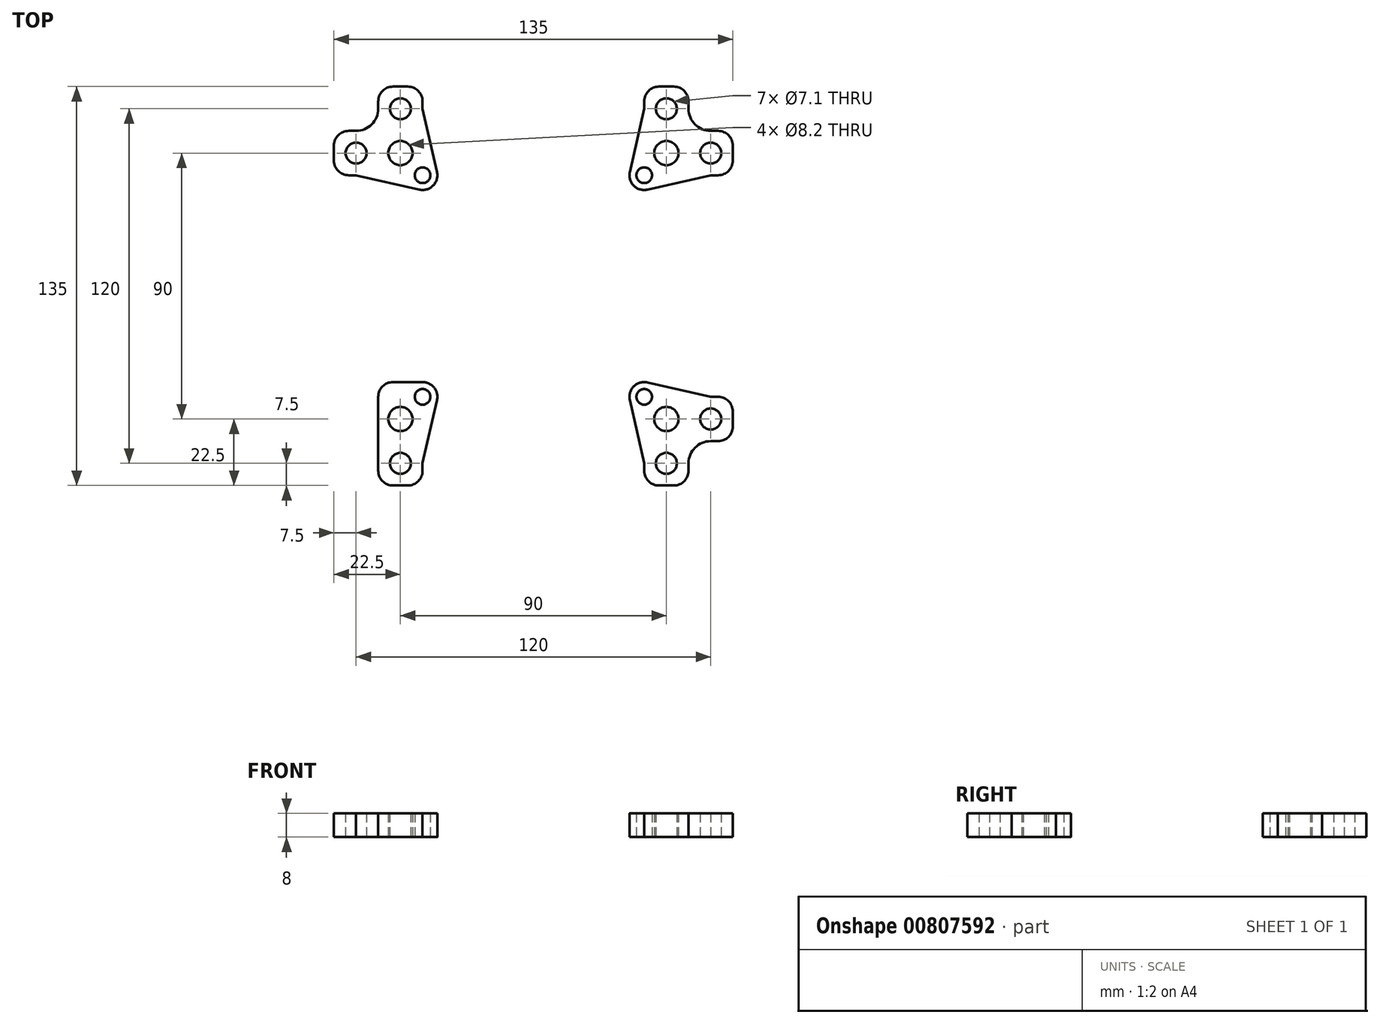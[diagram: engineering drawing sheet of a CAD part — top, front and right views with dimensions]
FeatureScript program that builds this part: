
annotation { "Feature Type Name" : "Feature", "Feature Type Description" : "" }
export const myFeature = defineFeature(function(context is Context, id is Id, definition is map)
    precondition{}
    {
        {
            var Q0;
            Q0=qCreatedBy(makeId("Top.planeOp"),FACE);
            var sketch = newSketch(context, id + "F0", { "sketchPlane" : qUnion([Q0])});
            skLineSegment(sketch, "E0.bottom", {"start": v(45, 45) * mm, "end": v(-45, 45) * mm, "construction": true});
            skLineSegment(sketch, "E0.top", {"start": v(45, -45) * mm, "end": v(-45, -45) * mm, "construction": true});
            skLineSegment(sketch, "E0.left", {"start": v(45, 45) * mm, "end": v(45, -45) * mm, "construction": true});
            skLineSegment(sketch, "E0.right", {"start": v(-45, 45) * mm, "end": v(-45, -45) * mm, "construction": true});
            skPoint(sketch, "E0.middle", {"position": v(0, 0) * mm});
            skCircle(sketch, "E1", {"center": v(-45, 45) * mm, "radius": 4.1 * mm});
            skCircle(sketch, "E2", {"center": v(45, 45) * mm, "radius": 4.1 * mm});
            skCircle(sketch, "E3", {"center": v(-45, -45) * mm, "radius": 4.1 * mm});
            skCircle(sketch, "E4", {"center": v(45, -45) * mm, "radius": 4.1 * mm});
            skLineSegment(sketch, "E5.bottom", {"start": v(37.5, 37.5) * mm, "end": v(-37.5, 37.5) * mm, "construction": true});
            skLineSegment(sketch, "E5.top", {"start": v(37.5, -37.5) * mm, "end": v(-37.5, -37.5) * mm, "construction": true});
            skLineSegment(sketch, "E5.left", {"start": v(37.5, 37.5) * mm, "end": v(37.5, -37.5) * mm, "construction": true});
            skLineSegment(sketch, "E5.right", {"start": v(-37.5, 37.5) * mm, "end": v(-37.5, -37.5) * mm, "construction": true});
            skCircle(sketch, "E6", {"center": v(-37.5, 37.5) * mm, "radius": 2.65 * mm});
            skCircle(sketch, "E7", {"center": v(37.5, 37.5) * mm, "radius": 2.65 * mm});
            skCircle(sketch, "E8", {"center": v(-37.5, -37.5) * mm, "radius": 2.65 * mm});
            skCircle(sketch, "E9", {"center": v(37.5, -37.5) * mm, "radius": 2.65 * mm});
            skCircle(sketch, "E10", {"center": v(-45, 60) * mm, "radius": 3.55 * mm});
            skCircle(sketch, "E11", {"center": v(-60, 45) * mm, "radius": 3.55 * mm});
            skCircle(sketch, "E12.MirrorC", {"center": v(45, 60) * mm, "radius": 3.55 * mm});
            skCircle(sketch, "E13.MirrorC", {"center": v(60, 45) * mm, "radius": 3.55 * mm});
            skCircle(sketch, "E14.MirrorC", {"center": v(-45, -60) * mm, "radius": 3.55 * mm});
            skCircle(sketch, "E15.MirrorC", {"center": v(45, -60) * mm, "radius": 3.55 * mm});
            skCircle(sketch, "E16.MirrorC", {"center": v(60, -45) * mm, "radius": 3.55 * mm});
            skLineSegment(sketch, "E17.bottom", {"start": v(-30, 52.5) * mm, "end": v(30, 52.5) * mm, "construction": true});
            skLineSegment(sketch, "E17.top", {"start": v(-30, -52.5) * mm, "end": v(30, -52.5) * mm, "construction": true});
            skLineSegment(sketch, "E17.left", {"start": v(-52.5, 30) * mm, "end": v(-52.5, -52.5) * mm, "construction": true});
            skLineSegment(sketch, "E17.right", {"start": v(52.5, 30) * mm, "end": v(52.5, -30) * mm, "construction": true});
            skLineSegment(sketch, "E18.top", {"start": v(-47.5, 67.5) * mm, "end": v(-42.5, 67.5) * mm});
            skLineSegment(sketch, "E18.left", {"start": v(-52.5, 60) * mm, "end": v(-52.5, 62.5) * mm});
            skLineSegment(sketch, "E18.right", {"start": v(-37.5, 60) * mm, "end": v(-37.5, 62.5) * mm});
            skLineSegment(sketch, "E19.bottom", {"start": v(-60, 52.5) * mm, "end": v(-62.5, 52.5) * mm});
            skLineSegment(sketch, "E19.top", {"start": v(-60, 37.5) * mm, "end": v(-62.5, 37.5) * mm});
            skLineSegment(sketch, "E19.right", {"start": v(-67.5, 47.5) * mm, "end": v(-67.5, 42.5) * mm});
            skLineSegment(sketch, "E20.MirrorCS", {"start": v(37.5, 60) * mm, "end": v(37.5, 62.5) * mm});
            skLineSegment(sketch, "E21.MirrorCS", {"start": v(47.5, 67.5) * mm, "end": v(42.5, 67.5) * mm});
            skLineSegment(sketch, "E22.MirrorCS", {"start": v(52.5, 60) * mm, "end": v(52.5, 62.5) * mm});
            skLineSegment(sketch, "E23.MirrorCS", {"start": v(60, 52.5) * mm, "end": v(62.5, 52.5) * mm});
            skLineSegment(sketch, "E24.MirrorCS", {"start": v(60, 37.5) * mm, "end": v(62.5, 37.5) * mm});
            skLineSegment(sketch, "E25.MirrorCS", {"start": v(67.5, 47.5) * mm, "end": v(67.5, 42.5) * mm});
            skLineSegment(sketch, "E26.MirrorCS", {"start": v(-52.5, -52.5) * mm, "end": v(-52.5, -62.5) * mm});
            skLineSegment(sketch, "E27.MirrorCS", {"start": v(-47.5, -67.5) * mm, "end": v(-42.5, -67.5) * mm});
            skLineSegment(sketch, "E28.MirrorCS", {"start": v(-37.5, -60) * mm, "end": v(-37.5, -62.5) * mm});
            skLineSegment(sketch, "E29.MirrorCS", {"start": v(37.5, -60) * mm, "end": v(37.5, -62.5) * mm});
            skLineSegment(sketch, "E30.MirrorCS", {"start": v(47.5, -67.5) * mm, "end": v(42.5, -67.5) * mm});
            skLineSegment(sketch, "E31.MirrorCS", {"start": v(52.5, -60) * mm, "end": v(52.5, -62.5) * mm});
            skLineSegment(sketch, "E32.MirrorCS", {"start": v(60, -52.5) * mm, "end": v(62.5, -52.5) * mm});
            skLineSegment(sketch, "E33.MirrorCS", {"start": v(67.5, -47.5) * mm, "end": v(67.5, -42.5) * mm});
            skLineSegment(sketch, "E34.MirrorCS", {"start": v(60, -37.5) * mm, "end": v(62.5, -37.5) * mm});
            skPoint(sketch, "E35.orphan", {"position": v(52.5, 52.5) * mm});
            skPoint(sketch, "E36.orphan", {"position": v(52.5, -52.5) * mm});
            skPoint(sketch, "E37.visualSharp", {"position": v(-52.5, 52.5) * mm});
            skArc(sketch, "E37.filletArc", {"start": v(-60, 52.5) * mm, "mid": v(-54.7, 54.7) * mm, "end": v(-52.5, 60) * mm});
            skArc(sketch, "E38.filletArc", {"start": v(52.5, 60) * mm, "mid": v(54.7, 54.7) * mm, "end": v(60, 52.5) * mm});
            skPoint(sketch, "E39.visualSharp", {"position": v(52.5, 37.5) * mm});
            skArc(sketch, "E39.filletArc", {"start": v(60, 37.5) * mm, "mid": v(54.7, 35.3) * mm, "end": v(52.5, 30) * mm, "construction": true});
            skPoint(sketch, "E40.visualSharp", {"position": v(52.5, -37.5) * mm});
            skArc(sketch, "E40.filletArc", {"start": v(52.5, -30) * mm, "mid": v(54.7, -35.3) * mm, "end": v(60, -37.5) * mm, "construction": true});
            skArc(sketch, "E41.filletArc", {"start": v(60, -52.5) * mm, "mid": v(54.7, -54.7) * mm, "end": v(52.5, -60) * mm});
            skPoint(sketch, "E42.visualSharp", {"position": v(37.5, -52.5) * mm});
            skArc(sketch, "E42.filletArc", {"start": v(37.5, -60) * mm, "mid": v(35.3, -54.7) * mm, "end": v(30, -52.5) * mm, "construction": true});
            skPoint(sketch, "E43.visualSharp", {"position": v(-37.5, -52.5) * mm});
            skArc(sketch, "E43.filletArc", {"start": v(-30, -52.5) * mm, "mid": v(-35.3, -54.7) * mm, "end": v(-37.5, -60) * mm, "construction": true});
            skPoint(sketch, "E44.visualSharp", {"position": v(-52.5, 37.5) * mm});
            skArc(sketch, "E44.filletArc", {"start": v(-52.5, 30) * mm, "mid": v(-54.7, 35.3) * mm, "end": v(-60, 37.5) * mm, "construction": true});
            skPoint(sketch, "E45.visualSharp", {"position": v(-37.5, 52.5) * mm});
            skArc(sketch, "E45.filletArc", {"start": v(-37.5, 60) * mm, "mid": v(-35.3, 54.7) * mm, "end": v(-30, 52.5) * mm, "construction": true});
            skPoint(sketch, "E46.visualSharp", {"position": v(37.5, 52.5) * mm});
            skArc(sketch, "E46.filletArc", {"start": v(30, 52.5) * mm, "mid": v(35.3, 54.7) * mm, "end": v(37.5, 60) * mm, "construction": true});
            skPoint(sketch, "E47.visualSharp", {"position": v(-52.5, -67.5) * mm});
            skArc(sketch, "E47.filletArc", {"start": v(-52.5, -62.5) * mm, "mid": v(-51.04, -66.04) * mm, "end": v(-47.5, -67.5) * mm});
            skPoint(sketch, "E48.visualSharp", {"position": v(-37.5, -67.5) * mm});
            skArc(sketch, "E48.filletArc", {"start": v(-42.5, -67.5) * mm, "mid": v(-38.96, -66.04) * mm, "end": v(-37.5, -62.5) * mm});
            skPoint(sketch, "E49.visualSharp", {"position": v(37.5, -67.5) * mm});
            skArc(sketch, "E49.filletArc", {"start": v(37.5, -62.5) * mm, "mid": v(38.96, -66.04) * mm, "end": v(42.5, -67.5) * mm});
            skPoint(sketch, "E50.visualSharp", {"position": v(52.5, -67.5) * mm});
            skArc(sketch, "E50.filletArc", {"start": v(47.5, -67.5) * mm, "mid": v(51.04, -66.04) * mm, "end": v(52.5, -62.5) * mm});
            skPoint(sketch, "E51.visualSharp", {"position": v(67.5, -52.5) * mm});
            skArc(sketch, "E51.filletArc", {"start": v(62.5, -52.5) * mm, "mid": v(66.04, -51.04) * mm, "end": v(67.5, -47.5) * mm});
            skPoint(sketch, "E52.visualSharp", {"position": v(67.5, -37.5) * mm});
            skArc(sketch, "E52.filletArc", {"start": v(67.5, -42.5) * mm, "mid": v(66.04, -38.96) * mm, "end": v(62.5, -37.5) * mm});
            skPoint(sketch, "E53.visualSharp", {"position": v(67.5, 37.5) * mm});
            skArc(sketch, "E53.filletArc", {"start": v(62.5, 37.5) * mm, "mid": v(66.04, 38.96) * mm, "end": v(67.5, 42.5) * mm});
            skPoint(sketch, "E54.visualSharp", {"position": v(67.5, 52.5) * mm});
            skArc(sketch, "E54.filletArc", {"start": v(67.5, 47.5) * mm, "mid": v(66.04, 51.04) * mm, "end": v(62.5, 52.5) * mm});
            skPoint(sketch, "E55.visualSharp", {"position": v(52.5, 67.5) * mm});
            skArc(sketch, "E55.filletArc", {"start": v(52.5, 62.5) * mm, "mid": v(51.04, 66.04) * mm, "end": v(47.5, 67.5) * mm});
            skPoint(sketch, "E56.visualSharp", {"position": v(37.5, 67.5) * mm});
            skArc(sketch, "E56.filletArc", {"start": v(42.5, 67.5) * mm, "mid": v(38.96, 66.04) * mm, "end": v(37.5, 62.5) * mm});
            skPoint(sketch, "E57.visualSharp", {"position": v(-52.5, 67.5) * mm});
            skArc(sketch, "E57.filletArc", {"start": v(-47.5, 67.5) * mm, "mid": v(-51.04, 66.04) * mm, "end": v(-52.5, 62.5) * mm});
            skPoint(sketch, "E58.visualSharp", {"position": v(-37.5, 67.5) * mm});
            skArc(sketch, "E58.filletArc", {"start": v(-37.5, 62.5) * mm, "mid": v(-38.96, 66.04) * mm, "end": v(-42.5, 67.5) * mm});
            skPoint(sketch, "E59.visualSharp", {"position": v(-67.5, 52.5) * mm});
            skArc(sketch, "E59.filletArc", {"start": v(-62.5, 52.5) * mm, "mid": v(-66.04, 51.04) * mm, "end": v(-67.5, 47.5) * mm});
            skPoint(sketch, "E60.visualSharp", {"position": v(-67.5, 37.5) * mm});
            skArc(sketch, "E60.filletArc", {"start": v(-67.5, 42.5) * mm, "mid": v(-66.04, 38.96) * mm, "end": v(-62.5, 37.5) * mm});
            skLineSegment(sketch, "E61", {"start": v(-60, 37.5) * mm, "end": v(-38.61, 32.63) * mm});
            skLineSegment(sketch, "E62", {"start": v(-32.63, 38.61) * mm, "end": v(-37.5, 60) * mm});
            skLineSegment(sketch, "E63", {"start": v(-52.5, 52.5) * mm, "end": v(-37.5, 37.5) * mm, "construction": true});
            skPoint(sketch, "E64.visualSharp", {"position": v(-30.86, 30.86) * mm});
            skArc(sketch, "E64.filletArc", {"start": v(-38.61, 32.63) * mm, "mid": v(-33.96, 33.96) * mm, "end": v(-32.63, 38.61) * mm});
            skArc(sketch, "E65.MirrorCS", {"start": v(38.61, 32.63) * mm, "mid": v(33.96, 33.96) * mm, "end": v(32.63, 38.61) * mm});
            skLineSegment(sketch, "E66.MirrorCS", {"start": v(32.63, 38.61) * mm, "end": v(37.5, 60) * mm});
            skLineSegment(sketch, "E67.MirrorCS", {"start": v(60, 37.5) * mm, "end": v(38.61, 32.63) * mm});
            skArc(sketch, "E68.MirrorCS", {"start": v(38.61, -32.63) * mm, "mid": v(33.96, -33.96) * mm, "end": v(32.63, -38.61) * mm});
            skLineSegment(sketch, "E69.MirrorCS", {"start": v(32.63, -38.61) * mm, "end": v(37.5, -60) * mm});
            skLineSegment(sketch, "E70.MirrorCS", {"start": v(60, -37.5) * mm, "end": v(38.61, -32.63) * mm});
            skLineSegment(sketch, "E71", {"start": v(-52.5, -52.5) * mm, "end": v(-52.5, -37.5) * mm});
            skLineSegment(sketch, "E72", {"start": v(-32.63, -38.61) * mm, "end": v(-37.5, -60) * mm});
            skLineSegment(sketch, "E73", {"start": v(-37.5, -32.5) * mm, "end": v(-47.5, -32.5) * mm});
            skPoint(sketch, "E74.visualSharp", {"position": v(-31.23, -32.5) * mm});
            skArc(sketch, "E74.filletArc", {"start": v(-32.63, -38.61) * mm, "mid": v(-33.6, -34.38) * mm, "end": v(-37.5, -32.5) * mm});
            skPoint(sketch, "E75.visualSharp", {"position": v(-52.5, -32.5) * mm});
            skArc(sketch, "E75.filletArc", {"start": v(-47.5, -32.5) * mm, "mid": v(-51.04, -33.96) * mm, "end": v(-52.5, -37.5) * mm});
            skSolve(sketch);
        }
        {
            var Q0;
            Q0=makeQuery(id+"F0.imprint","IMPRINT",FACE,{"disambiguationData":[TD([[makeQuery(id+"F0.imprint","IMPRINT",EDGE,{"derivedFrom":sQuery(id+"F0.wireOp",EDGE,"E1")}),-1.0]])]});
            var Q1;
            Q1=makeQuery(id+"F0.imprint","IMPRINT",FACE,{"disambiguationData":[TD([[makeQuery(id+"F0.imprint","IMPRINT",EDGE,{"derivedFrom":sQuery(id+"F0.wireOp",EDGE,"E2")}),-1.0]])]});
            var Q2;
            Q2=makeQuery(id+"F0.imprint","IMPRINT",FACE,{"disambiguationData":[TD([[makeQuery(id+"F0.imprint","IMPRINT",EDGE,{"derivedFrom":sQuery(id+"F0.wireOp",EDGE,"E3")}),-1.0]])]});
            var Q3;
            Q3=makeQuery(id+"F0.imprint","IMPRINT",FACE,{"disambiguationData":[TD([[makeQuery(id+"F0.imprint","IMPRINT",EDGE,{"derivedFrom":sQuery(id+"F0.wireOp",EDGE,"E4")}),-1.0]])]});
            extrude(context, id + "F1", {"entities" : qUnion([Q0, Q1, Q2, Q3]), "depth" : 8 * mm, "offsetDistance" : 25 * mm});
        }
    });
